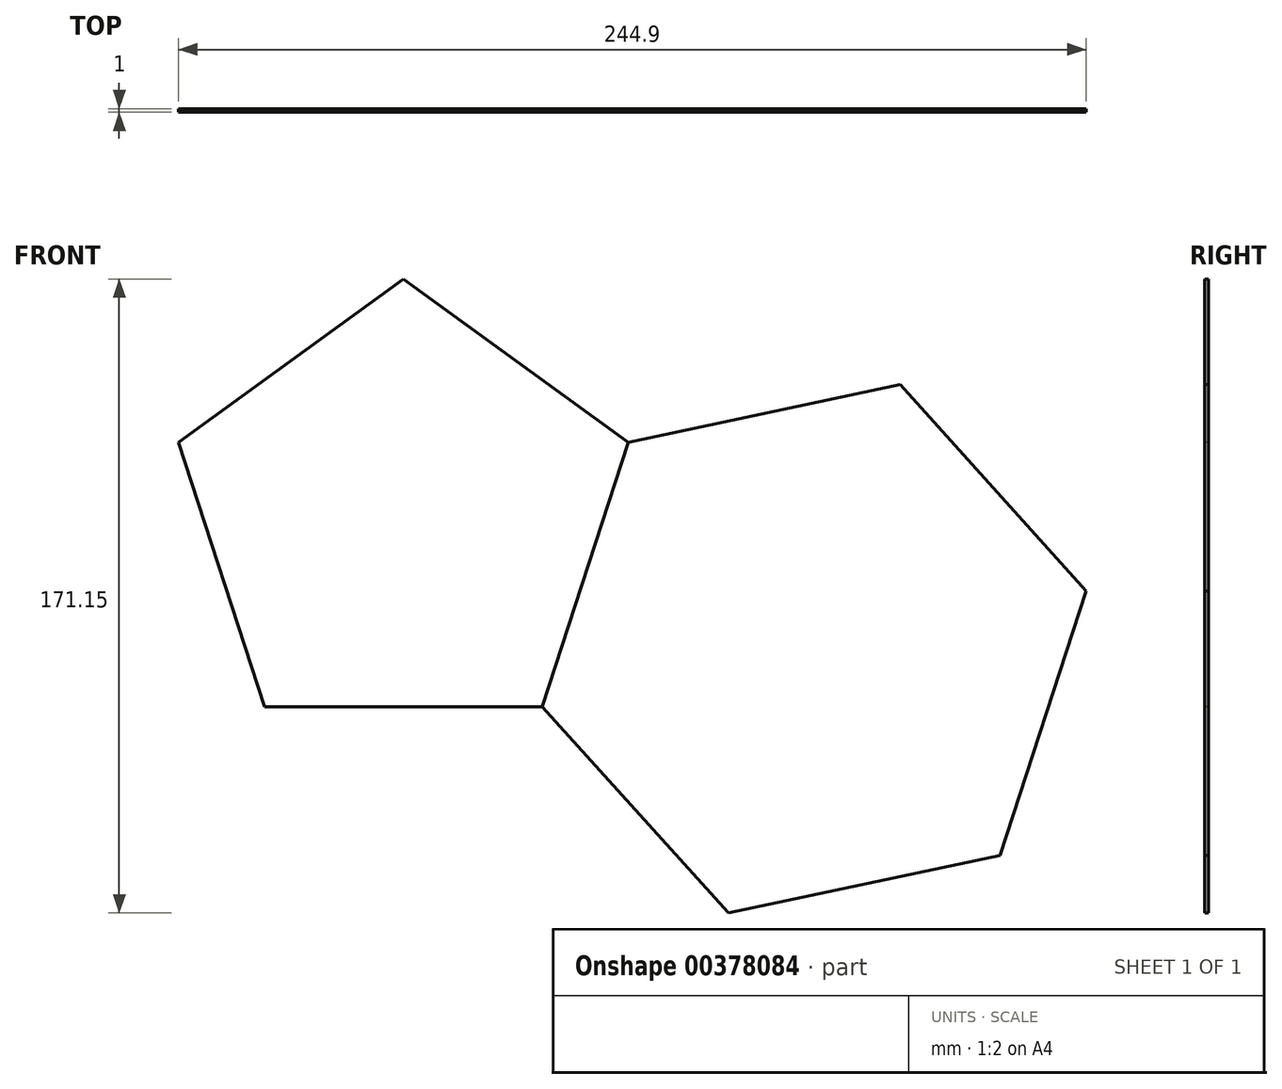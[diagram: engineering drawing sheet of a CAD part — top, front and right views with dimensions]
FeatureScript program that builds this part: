
annotation { "Feature Type Name" : "Feature", "Feature Type Description" : "" }
export const myFeature = defineFeature(function(context is Context, id is Id, definition is map)
    precondition{}
    {
        {
            var Q0;
            Q0=qCreatedBy(makeId("Front.planeOp"),FACE);
            var sketch = newSketch(context, id + "F0", { "sketchPlane" : qUnion([Q0])});
            skCircle(sketch, "E0.cCircle", {"center": v(0, 0) * mm, "radius": 51.61 * mm, "construction": true});
            skLineSegment(sketch, "E0.0", {"start": v(37.5, -51.61) * mm, "end": v(-37.5, -51.61) * mm});
            skLineSegment(sketch, "E0.1", {"start": v(-37.5, -51.61) * mm, "end": v(-60.68, 19.71) * mm});
            skLineSegment(sketch, "E0.2", {"start": v(-60.68, 19.71) * mm, "end": v(0, 63.8) * mm});
            skLineSegment(sketch, "E0.3", {"start": v(0, 63.8) * mm, "end": v(60.68, 19.71) * mm});
            skLineSegment(sketch, "E0.4", {"start": v(60.68, 19.71) * mm, "end": v(37.5, -51.61) * mm});
            skPoint(sketch, "E0.0.midPoint", {"position": v(0, -51.61) * mm});
            skCircle(sketch, "E1.cCircle", {"center": v(110.86, -36.02) * mm, "radius": 64.95 * mm, "construction": true});
            skLineSegment(sketch, "E1.0", {"start": v(134.04, 35.3) * mm, "end": v(184.22, -20.43) * mm});
            skLineSegment(sketch, "E1.1", {"start": v(184.22, -20.43) * mm, "end": v(161.05, -91.76) * mm});
            skLineSegment(sketch, "E1.2", {"start": v(161.05, -91.76) * mm, "end": v(87.68, -107.35) * mm});
            skLineSegment(sketch, "E1.3", {"start": v(87.68, -107.35) * mm, "end": v(37.5, -51.61) * mm});
            skLineSegment(sketch, "E1.4", {"start": v(37.5, -51.61) * mm, "end": v(60.68, 19.71) * mm});
            skLineSegment(sketch, "E1.5", {"start": v(60.68, 19.71) * mm, "end": v(134.04, 35.3) * mm});
            skPoint(sketch, "E1.0.midPoint", {"position": v(159.13, 7.44) * mm});
            skSolve(sketch);
        }
        {
            var Q0;
            Q0=makeQuery(id+"F0.imprint","IMPRINT",FACE,{"disambiguationData":[TD([[makeQuery(id+"F0.imprint","IMPRINT",EDGE,{"derivedFrom":sQuery(id+"F0.wireOp",EDGE,"E0.1")}),-1.0]])]});
            extrude(context, id + "F1", {"entities" : qUnion([Q0]), "oppositeDirection" : true, "depth" : 1 * mm});
        }
        {
            var Q0;
            Q0=makeQuery(id+"F0.imprint","IMPRINT",FACE,{"disambiguationData":[TD([[makeQuery(id+"F0.imprint","IMPRINT",EDGE,{"derivedFrom":sQuery(id+"F0.wireOp",EDGE,"E1.0")}),-1.0]])]});
            extrude(context, id + "F2", {"entities" : qUnion([Q0]), "oppositeDirection" : true, "depth" : 1 * mm});
        }
    });
